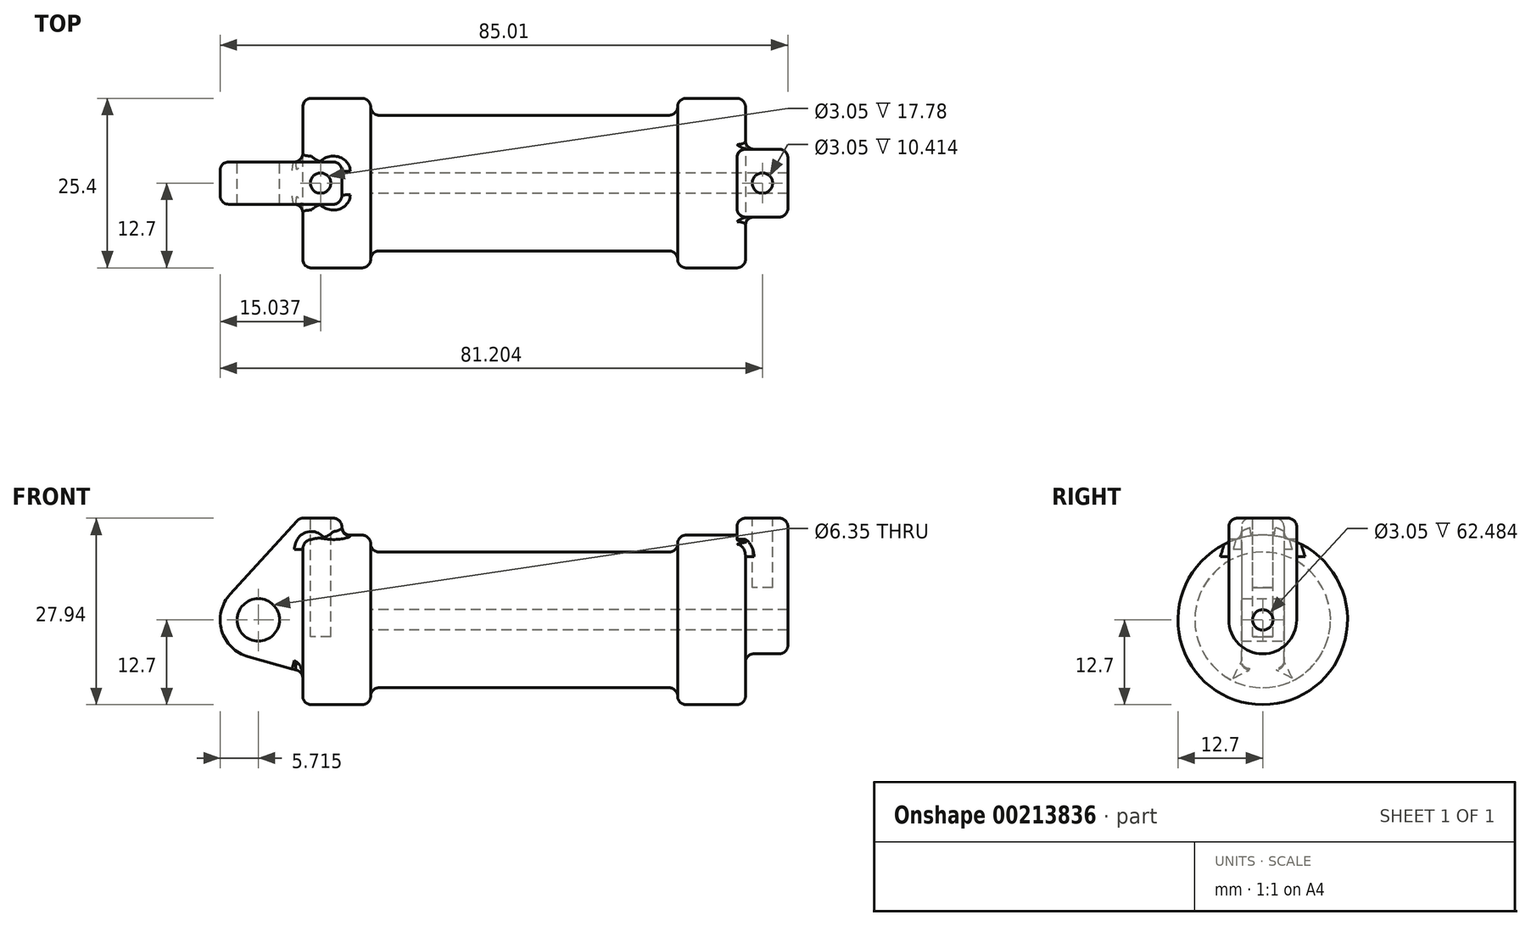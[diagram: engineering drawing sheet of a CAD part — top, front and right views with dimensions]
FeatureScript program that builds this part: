
annotation { "Feature Type Name" : "Feature", "Feature Type Description" : "" }
export const myFeature = defineFeature(function(context is Context, id is Id, definition is map)
    precondition{}
    {
        {
            var Q0;
            Q0=qCreatedBy(makeId("Front.planeOp"),FACE);
            var sketch = newSketch(context, id + "F0", { "sketchPlane" : qUnion([Q0])});
            skLineSegment(sketch, "E0", {"start": v(0, 0) * mm, "end": v(0, 12.7) * mm});
            skLineSegment(sketch, "E1", {"start": v(0, 12.7) * mm, "end": v(10.16, 12.7) * mm});
            skLineSegment(sketch, "E2", {"start": v(10.16, 12.7) * mm, "end": v(10.16, 10.16) * mm});
            skLineSegment(sketch, "E3", {"start": v(10.16, 10.16) * mm, "end": v(56.13, 10.16) * mm});
            skLineSegment(sketch, "E4", {"start": v(56.13, 10.16) * mm, "end": v(56.13, 12.7) * mm});
            skLineSegment(sketch, "E5", {"start": v(56.13, 12.7) * mm, "end": v(66.3, 12.7) * mm});
            skLineSegment(sketch, "E6", {"start": v(66.3, 12.7) * mm, "end": v(66.3, 0) * mm});
            skLineSegment(sketch, "E7", {"start": v(66.3, 0) * mm, "end": v(0, 0) * mm});
            skLineSegment(sketch, "E8", {"start": v(5.84, 15.24) * mm, "end": v(-0.5, 15.24) * mm});
            skLineSegment(sketch, "E9", {"start": v(-0.5, 15.24) * mm, "end": v(-10.88, 3.85) * mm});
            skLineSegment(sketch, "E10", {"start": v(0, 0) * mm, "end": v(-6.65, 0) * mm});
            skCircle(sketch, "E11", {"center": v(-6.65, 0) * mm, "radius": 5.72 * mm});
            skCircle(sketch, "E12", {"center": v(-6.65, 0) * mm, "radius": 3.18 * mm});
            skLineSegment(sketch, "E13", {"start": v(5.84, 15.24) * mm, "end": v(5.84, -9.4) * mm});
            skLineSegment(sketch, "E14", {"start": v(5.84, -9.4) * mm, "end": v(-8.18, -5.5) * mm});
            skSolve(sketch);
        }
        {
            var Q0;
            {var subQ0=sQuery(id+"F0.wireOp",EDGE,"E2");Q0=makeQuery(id+"F0.imprint","IMPRINT",FACE,{"disambiguationData":[TD([[makeQuery(id+"F0.imprint","IMPRINT",EDGE,{"derivedFrom":subQ0}),-1.0]])]});}
            var Q1;
            {var subQ0=sQuery(id+"F0.wireOp",EDGE,"E0");Q1=makeQuery(id+"F0.imprint","IMPRINT",FACE,{"disambiguationData":[TD([[makeQuery(id+"F0.imprint","IMPRINT",EDGE,{"derivedFrom":subQ0}),-1.0]])]});}
            var Q2;
            Q2=sQuery(id+"F0.wireOp",EDGE,"E7");
            revolve(context, id + "F1", {"entities" : qUnion([Q0, Q1]), "axis" : qUnion([Q2]), "revolveType" : RevolveType.FULL});
        }
        {
            var Q0;
            {var subQ0=sQuery(id+"F0.wireOp",EDGE,"E0");Q0=makeQuery(id+"F0.imprint","IMPRINT",FACE,{"disambiguationData":[TD([[makeQuery(id+"F0.imprint","IMPRINT",EDGE,{"derivedFrom":subQ0}),-1.0]])]});}
            var Q1;
            {var subQ3=sQuery(id+"F0.wireOp",EDGE,"E0");Q1=makeQuery(id+"F0.imprint","IMPRINT",FACE,{"disambiguationData":[TD([[makeQuery(id+"F0.imprint","IMPRINT",EDGE,{"derivedFrom":subQ3}),1.0]])]});}
            var Q2;
            {var subQ0=sQuery(id+"F0.wireOp",EDGE,"E14");Q2=makeQuery(id+"F0.imprint","IMPRINT",FACE,{"disambiguationData":[TD([[makeQuery(id+"F0.imprint","IMPRINT",EDGE,{"derivedFrom":subQ0}),-1.0]])]});}
            var Q3;
            {var subQ4=sQuery(id+"F0.wireOp",EDGE,"E12");Q3=makeQuery(id+"F0.imprint","IMPRINT",FACE,{"disambiguationData":[TD([[makeQuery(id+"F0.imprint","IMPRINT",EDGE,{"derivedFrom":subQ4}),-1.0]])]});}
            extrude(context, id + "F2", {"entities" : qUnion([Q0, Q1, Q2, Q3]), "operationType" : NewBodyOperationType.ADD, "endBound" : BoundingType.SYMMETRIC, "depth" : 6.35 * mm});
        }
        {
            var Q0;
            Q0=makeQuery(id+"F1.opRevolve","SWEPT_FACE",FACE,{"disambiguationData":[OSD([sQuery(id+"F0.wireOp",EDGE,"E6")])]});
            var sketch = newSketch(context, id + "F3", { "sketchPlane" : qUnion([Q0])});
            skCircle(sketch, "E15", {"center": v(0, 0) * mm, "radius": 1.52 * mm});
            skCircle(sketch, "E16", {"center": v(0, 0) * mm, "radius": 5.08 * mm});
            skLineSegment(sketch, "E17", {"start": v(5.08, 0) * mm, "end": v(5.08, 15.24) * mm});
            skLineSegment(sketch, "E18", {"start": v(5.08, 15.24) * mm, "end": v(-5.08, 15.24) * mm});
            skLineSegment(sketch, "E19", {"start": v(-5.08, 15.24) * mm, "end": v(-5.08, 0) * mm});
            skSolve(sketch);
        }
        {
            var Q0;
            {var subQ0=sQuery(id+"F3.wireOp",EDGE,"E17");var subQ1=sQuery(id+"F3.wireOp",EDGE,"E16");var subQ2=makeQuery(id+"F3.imprint","INTERSECT",VERTEX,{"derivedFrom":[subQ1,subQ0]});Q0=makeQuery(id+"F3.imprint","IMPRINT",FACE,{"disambiguationData":[TD([[makeQuery(id+"F3.imprint","IMPRINT",EDGE,{"disambiguationData":[TD([[subQ2,-1.0]])],"derivedFrom":subQ1}),-1.0]])]});}
            var Q1;
            Q1=makeQuery(id+"F3.imprint","IMPRINT",FACE,{"disambiguationData":[TD([[makeQuery(id+"F3.imprint","IMPRINT",EDGE,{"derivedFrom":sQuery(id+"F3.wireOp",EDGE,"E15")}),-1.0]])]});
            var Q2;
            {var subQ0=sQuery(id+"F3.wireOp",EDGE,"E18");Q2=makeQuery(id+"F3.imprint","IMPRINT",FACE,{"disambiguationData":[TD([[makeQuery(id+"F3.imprint","IMPRINT",EDGE,{"derivedFrom":subQ0}),1.0]])]});}
            extrude(context, id + "F4", {"entities" : qUnion([Q0, Q1, Q2]), "operationType" : NewBodyOperationType.ADD, "depth" : 6.35 * mm, "hasSecondDirection" : true, "secondDirectionOppositeDirection" : true, "secondDirectionDepth" : 1.27 * mm});
        }
        {
            var Q0;
            Q0=makeQuery(id+"F3.imprint","IMPRINT",FACE,{"disambiguationData":[TD([[makeQuery(id+"F3.imprint","IMPRINT",EDGE,{"derivedFrom":sQuery(id+"F3.wireOp",EDGE,"E15")}),1.0]])]});
            var Q1;
            Q1=makeQuery(id+"F1.opRevolve","SWEPT_FACE",FACE,{"disambiguationData":[OSD([sQuery(id+"F0.wireOp",EDGE,"E2")])]});
            extrude(context, id + "F5", {"entities" : qUnion([Q0]), "operationType" : NewBodyOperationType.REMOVE, "endBound" : BoundingType.UP_TO_SURFACE, "oppositeDirection" : true, "endBoundEntityFace" : qUnion([Q1]), "depth" : 25.4 * mm});
        }
        {
            var Q0;
            Q0=makeQuery(id+"F4.opExtrude","SWEPT_FACE",FACE,{"disambiguationData":[OSD([sQuery(id+"F3.wireOp",EDGE,"E18")])]});
            var sketch = newSketch(context, id + "F6", { "sketchPlane" : qUnion([Q0])});
            skLineSegment(sketch, "E20", {"start": v(65.02, 5.08) * mm, "end": v(72.64, -5.08) * mm, "construction": true});
            skLineSegment(sketch, "E21", {"start": v(65.02, -5.08) * mm, "end": v(72.64, 5.08) * mm, "construction": true});
            skLineSegment(sketch, "E22", {"start": v(5.84, -3.18) * mm, "end": v(-0.5, 3.18) * mm, "construction": true});
            skLineSegment(sketch, "E23", {"start": v(5.84, 3.18) * mm, "end": v(-0.5, -3.17) * mm, "construction": true});
            skCircle(sketch, "E24", {"center": v(2.67, 0) * mm, "radius": 1.52 * mm});
            skCircle(sketch, "E25", {"center": v(68.83, 0) * mm, "radius": 1.52 * mm});
            skSolve(sketch);
        }
        {
            var Q0;
            Q0=makeQuery(id+"F6.imprint","IMPRINT",FACE,{"disambiguationData":[TD([[makeQuery(id+"F6.imprint","IMPRINT",EDGE,{"derivedFrom":sQuery(id+"F6.wireOp",EDGE,"E24")}),1.0]])]});
            extrude(context, id + "F7", {"entities" : qUnion([Q0]), "operationType" : NewBodyOperationType.REMOVE, "oppositeDirection" : true, "depth" : 17.78 * mm});
        }
        {
            var Q0;
            Q0=makeQuery(id+"F6.imprint","IMPRINT",FACE,{"disambiguationData":[TD([[makeQuery(id+"F6.imprint","IMPRINT",EDGE,{"derivedFrom":sQuery(id+"F6.wireOp",EDGE,"E25")}),1.0]])]});
            extrude(context, id + "F8", {"entities" : qUnion([Q0]), "operationType" : NewBodyOperationType.REMOVE, "oppositeDirection" : true, "depth" : 10.4 * mm});
        }
        {
            var Q0;
            Q0=makeQuery(id+"F1.opRevolve","SWEPT_FACE",FACE,{"disambiguationData":[OSD([sQuery(id+"F0.wireOp",EDGE,"E2")])]});
            var Q1;
            Q1=makeQuery(id+"F1.opRevolve","SWEPT_FACE",FACE,{"disambiguationData":[OSD([sQuery(id+"F0.wireOp",EDGE,"E4")])]});
            var Q2;
            Q2=makeQuery(id+"F1.opRevolve","SWEPT_FACE",FACE,{"disambiguationData":[OSD([sQuery(id+"F0.wireOp",EDGE,"E0")])]});
            var Q3;
            Q3=makeQuery(id+"F4.boolean.opBoolean","SPLIT",FACE,{"disambiguationData":[TD([makeQuery(id+"F1.opRevolve","SWEPT_FACE",FACE,{"disambiguationData":[OSD([sQuery(id+"F0.wireOp",EDGE,"E5")])]})])],"derivedFrom":makeQuery(id+"F1.opRevolve","SWEPT_FACE",FACE,{"disambiguationData":[OSD([sQuery(id+"F0.wireOp",EDGE,"E6")])]})});
            fillet(context, id + "F9", {"entities" : qUnion([Q0, Q1, Q2, Q3]), "radius" : 1.27 * mm, "tangentPropagation" : true, "allowEdgeOverflow" : false});
        }
        {
            var Q0;
            Q0=makeQuery(id+"F2.opExtrude","CAP_EDGE",EDGE,{"disambiguationData":[OSD([sQuery(id+"F0.wireOp",EDGE,"E11")])],"isStart":false});
            var Q1;
            Q1=makeQuery(id+"F2.opExtrude","CAP_EDGE",EDGE,{"disambiguationData":[OSD([sQuery(id+"F0.wireOp",EDGE,"E11")])],"isStart":true});
            var Q2;
            Q2=makeQuery(id+"F2.opExtrude","CAP_EDGE",EDGE,{"disambiguationData":[OSD([sQuery(id+"F0.wireOp",EDGE,"E8")])],"isStart":false});
            var Q3;
            Q3=makeQuery(id+"F2.opExtrude","SWEPT_EDGE",EDGE,{"disambiguationData":[OSD([sQuery(id+"F0.wireOp",EDGE,"E8"),sQuery(id+"F0.wireOp",EDGE,"E9")])]});
            var Q4;
            Q4=makeQuery(id+"F2.opExtrude","CAP_EDGE",EDGE,{"disambiguationData":[OSD([sQuery(id+"F0.wireOp",EDGE,"E8")])],"isStart":true});
            var Q5;
            Q5=makeQuery(id+"F2.opExtrude","SWEPT_EDGE",EDGE,{"disambiguationData":[OSD([sQuery(id+"F0.wireOp",EDGE,"E8"),sQuery(id+"F0.wireOp",EDGE,"E13")])]});
            var Q6;
            Q6=makeQuery(id+"F2.boolean.opBoolean","INTERSECT",EDGE,{"derivedFrom":[makeQuery(id+"F1.opRevolve","SWEPT_FACE",FACE,{"disambiguationData":[OSD([sQuery(id+"F0.wireOp",EDGE,"E1")])]}),makeQuery(id+"F2.opExtrude","SWEPT_FACE",FACE,{"disambiguationData":[OSD([sQuery(id+"F0.wireOp",EDGE,"E13")])]})]});
            var Q7;
            Q7=makeQuery(id+"F2.opExtrude","CAP_EDGE",EDGE,{"disambiguationData":[OSD([sQuery(id+"F0.wireOp",EDGE,"E13")])],"isStart":true});
            var Q8;
            Q8=makeQuery(id+"F2.opExtrude","CAP_EDGE",EDGE,{"disambiguationData":[OSD([sQuery(id+"F0.wireOp",EDGE,"E13")])],"isStart":false});
            var Q9;
            Q9=makeQuery(id+"F2.opExtrude","CAP_EDGE",EDGE,{"disambiguationData":[OSD([sQuery(id+"F0.wireOp",EDGE,"E14")])],"isStart":true});
            var Q10;
            Q10=makeQuery(id+"F2.opExtrude","CAP_EDGE",EDGE,{"disambiguationData":[OSD([sQuery(id+"F0.wireOp",EDGE,"E14")])],"isStart":false});
            fillet(context, id + "F10", {"entities" : qUnion([Q0, Q1, Q2, Q3, Q4, Q5, Q6, Q7, Q8, Q9, Q10]), "radius" : 1.27 * mm, "tangentPropagation" : true, "allowEdgeOverflow" : false});
        }
        {
            var Q0;
            Q0=makeQuery(id+"F4.opExtrude","SWEPT_EDGE",EDGE,{"disambiguationData":[OSD([sQuery(id+"F3.wireOp",EDGE,"E18"),sQuery(id+"F3.wireOp",EDGE,"E19")])]});
            var Q1;
            Q1=makeQuery(id+"F4.opExtrude","CAP_EDGE",EDGE,{"disambiguationData":[OSD([sQuery(id+"F3.wireOp",EDGE,"E18")])],"isStart":false});
            var Q2;
            Q2=makeQuery(id+"F4.opExtrude","CAP_EDGE",EDGE,{"disambiguationData":[OSD([sQuery(id+"F3.wireOp",EDGE,"E18")])],"isStart":true});
            var Q3;
            Q3=makeQuery(id+"F4.opExtrude","SWEPT_EDGE",EDGE,{"disambiguationData":[OSD([sQuery(id+"F3.wireOp",EDGE,"E17"),sQuery(id+"F3.wireOp",EDGE,"E18")])]});
            var Q4;
            Q4=makeQuery(id+"F4.opExtrude","CAP_EDGE",EDGE,{"disambiguationData":[OSD([sQuery(id+"F3.wireOp",EDGE,"E19")])],"isStart":true});
            var Q5;
            Q5=makeQuery(id+"F4.opExtrude","CAP_EDGE",EDGE,{"disambiguationData":[OSD([sQuery(id+"F3.wireOp",EDGE,"E19")])],"isStart":false});
            var Q6;
            Q6=makeQuery(id+"F4.opExtrude","CAP_EDGE",EDGE,{"disambiguationData":[OSD([sQuery(id+"F3.wireOp",EDGE,"E17")])],"isStart":true});
            fillet(context, id + "F11", {"entities" : qUnion([Q0, Q1, Q2, Q3, Q4, Q5, Q6]), "radius" : 1.27 * mm, "tangentPropagation" : true, "allowEdgeOverflow" : false});
        }
    });
